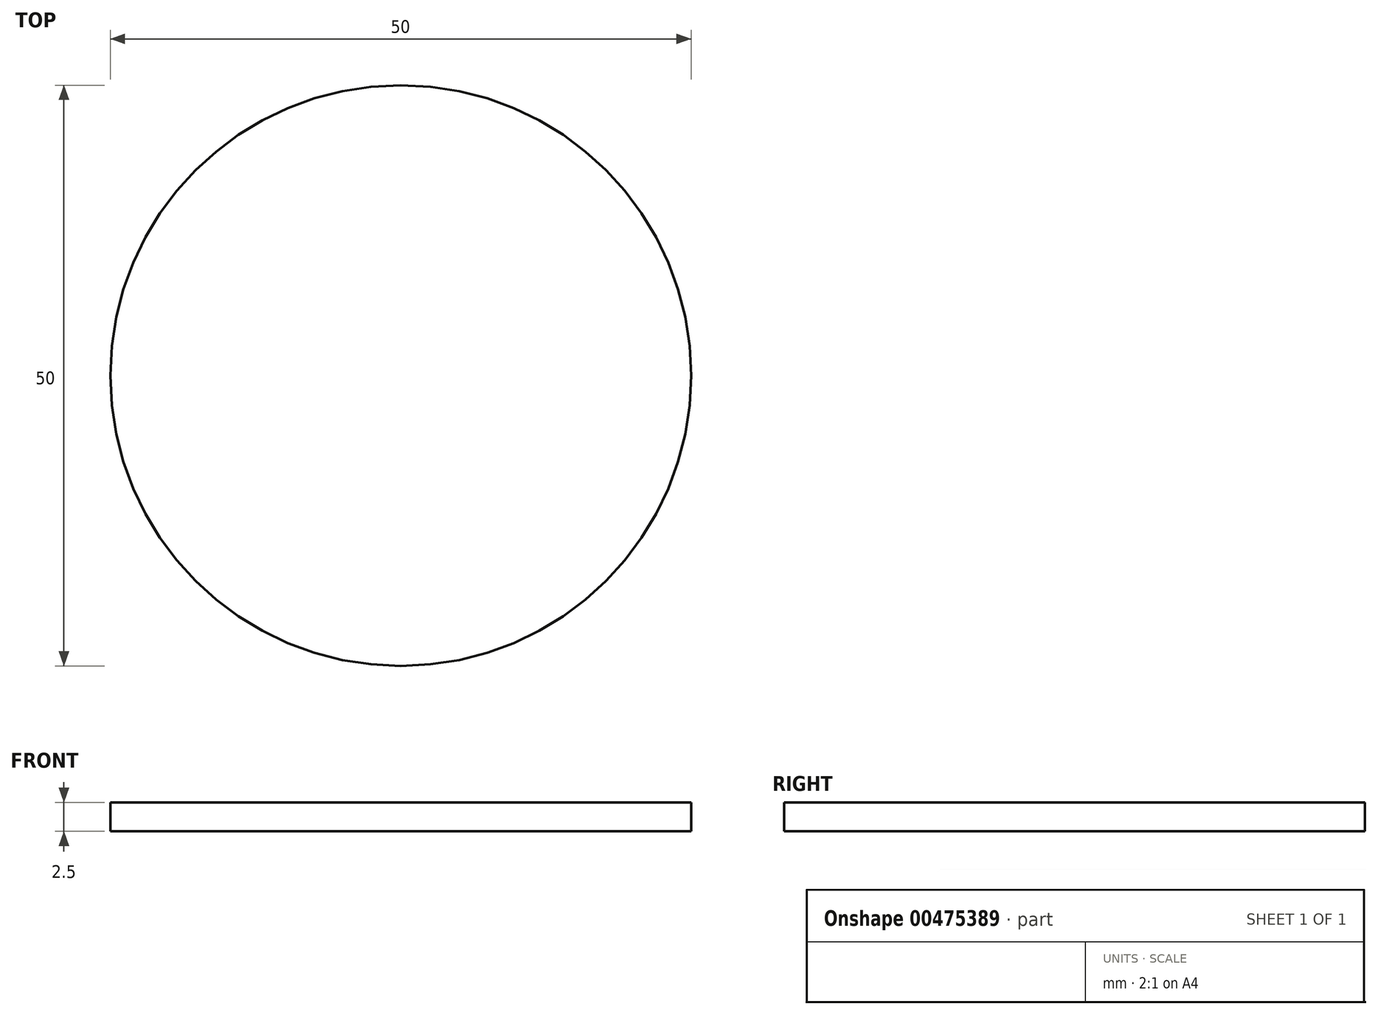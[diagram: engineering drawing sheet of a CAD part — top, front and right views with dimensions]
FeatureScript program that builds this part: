
annotation { "Feature Type Name" : "Feature", "Feature Type Description" : "" }
export const myFeature = defineFeature(function(context is Context, id is Id, definition is map)
    precondition{}
    {
        {
            var Q0;
            Q0=qCreatedBy(makeId("Top.planeOp"),FACE);
            var sketch = newSketch(context, id + "F0", { "sketchPlane" : qUnion([Q0])});
            skLineSegment(sketch, "E0.bottom", {"start": v(150, -100) * mm, "end": v(-150, -100) * mm});
            skLineSegment(sketch, "E0.top", {"start": v(150, 100) * mm, "end": v(-150, 100) * mm});
            skLineSegment(sketch, "E0.left", {"start": v(150, -100) * mm, "end": v(150, 100) * mm});
            skLineSegment(sketch, "E0.right", {"start": v(-150, -100) * mm, "end": v(-150, 100) * mm});
            skPoint(sketch, "E0.middle", {"position": v(0, 0) * mm});
            skSolve(sketch);
        }
        {
            var Q0;
            Q0 = qSketchRegion(id + "F0", true);
            var sketch = newSketch(context, id + "F1", { "sketchPlane" : qUnion([Q0])});
            skCircle(sketch, "E1", {"center": v(0, 0) * mm, "radius": 25 * mm});
            skSolve(sketch);
        }
        {
            var Q0;
            Q0=makeQuery(id+"F1.imprint","IMPRINT",FACE,{"disambiguationData":[TD([[makeQuery(id+"F1.imprint","IMPRINT",EDGE,{"derivedFrom":sQuery(id+"F1.wireOp",EDGE,"E1")}),1.0]])]});
            var Q1;
            Q1 = qSketchRegion(id + "F1", true);
            extrude(context, id + "F2", {"entities" : qUnion([Q0, Q1]), "depth" : 2.5 * mm, "offsetDistance" : 25 * mm});
        }
    });
